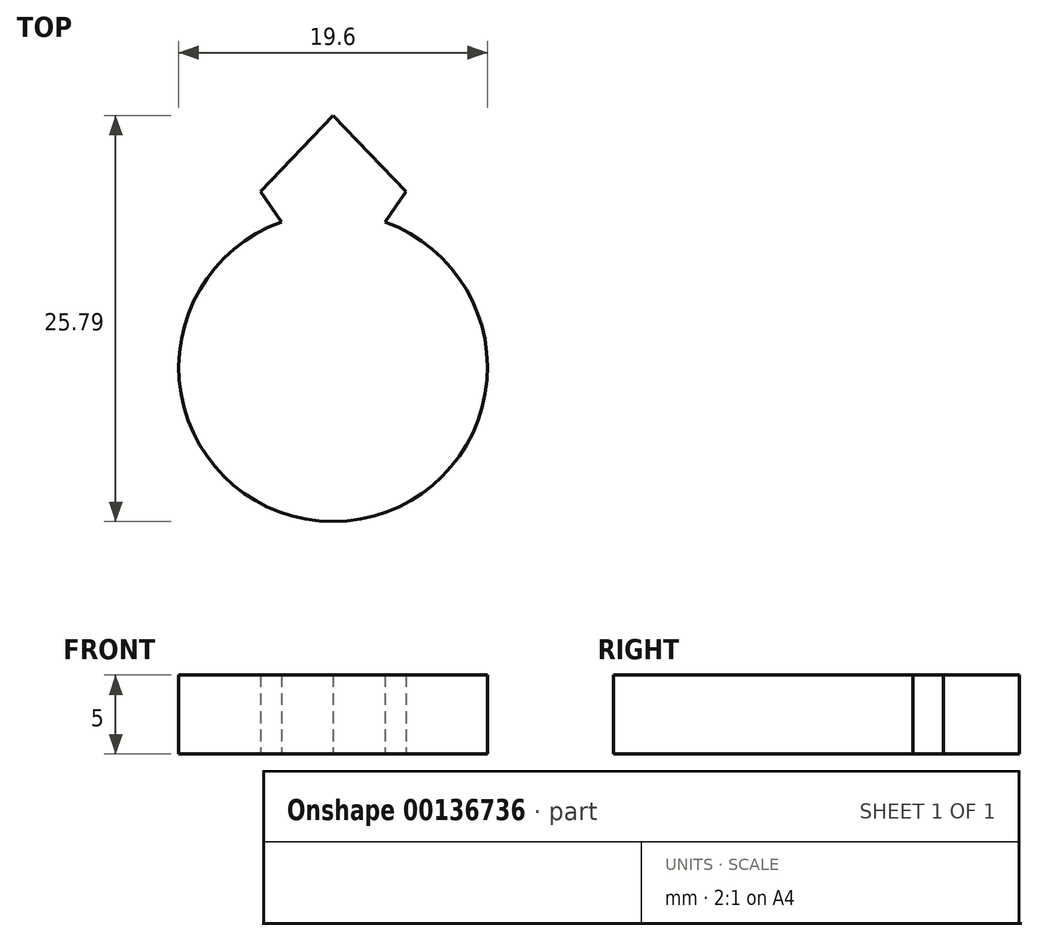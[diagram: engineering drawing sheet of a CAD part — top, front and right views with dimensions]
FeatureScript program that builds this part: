
annotation { "Feature Type Name" : "Feature", "Feature Type Description" : "" }
export const myFeature = defineFeature(function(context is Context, id is Id, definition is map)
    precondition{}
    {
        {
            var Q0;
            Q0=qCreatedBy(makeId("Top.planeOp"),FACE);
            var sketch = newSketch(context, id + "F0", { "sketchPlane" : qUnion([Q0])});
            skLineSegment(sketch, "E0", {"start": v(-2, 8.77) * mm, "end": v(-3.59, 11.08) * mm});
            skLineSegment(sketch, "E1", {"start": v(-3.59, 11.08) * mm, "end": v(0, 14.84) * mm});
            skLineSegment(sketch, "E2", {"start": v(0, 14.84) * mm, "end": v(3.59, 11.08) * mm});
            skLineSegment(sketch, "E3", {"start": v(3.59, 11.08) * mm, "end": v(2, 8.77) * mm});
            skLineSegment(sketch, "E4", {"start": v(0, 0) * mm, "end": v(0, 14.84) * mm, "construction": true});
            skArc(sketch, "E5", {"start": v(-2, 8.77) * mm, "mid": v(0, -9) * mm, "end": v(2, 8.77) * mm});
            skArc(sketch, "E6", {"start": v(2, 8.77) * mm, "mid": v(0, 9) * mm, "end": v(-2, 8.77) * mm});
            skLineSegment(sketch, "E7.0", {"start": v(4.62, 11.16) * mm, "end": v(3.29, 9.23) * mm});
            skArc(sketch, "E7.1", {"start": v(-3.29, 9.23) * mm, "mid": v(0, -9.8) * mm, "end": v(3.29, 9.23) * mm});
            skLineSegment(sketch, "E7.2", {"start": v(0, 16) * mm, "end": v(4.62, 11.16) * mm});
            skLineSegment(sketch, "E7.3", {"start": v(-4.62, 11.16) * mm, "end": v(0, 16) * mm});
            skLineSegment(sketch, "E7.4", {"start": v(-3.29, 9.23) * mm, "end": v(-4.62, 11.16) * mm});
            skSolve(sketch);
        }
        {
            var Q0;
            Q0=makeQuery(id+"F0.imprint","IMPRINT",FACE,{"disambiguationData":[TD([[makeQuery(id+"F0.imprint","IMPRINT",EDGE,{"derivedFrom":sQuery(id+"F0.wireOp",EDGE,"E5")}),1.0]])]});
            var Q1;
            Q1=makeQuery(id+"F0.imprint","IMPRINT",FACE,{"disambiguationData":[TD([[makeQuery(id+"F0.imprint","IMPRINT",EDGE,{"derivedFrom":sQuery(id+"F0.wireOp",EDGE,"E0")}),-1.0]])]});
            var Q2;
            Q2=makeQuery(id+"F0.imprint","IMPRINT",FACE,{"disambiguationData":[TD([[makeQuery(id+"F0.imprint","IMPRINT",EDGE,{"derivedFrom":sQuery(id+"F0.wireOp",EDGE,"E0")}),1.0]])]});
            extrude(context, id + "F1", {"entities" : qUnion([Q0, Q1, Q2]), "depth" : 5 * mm});
        }
    });
